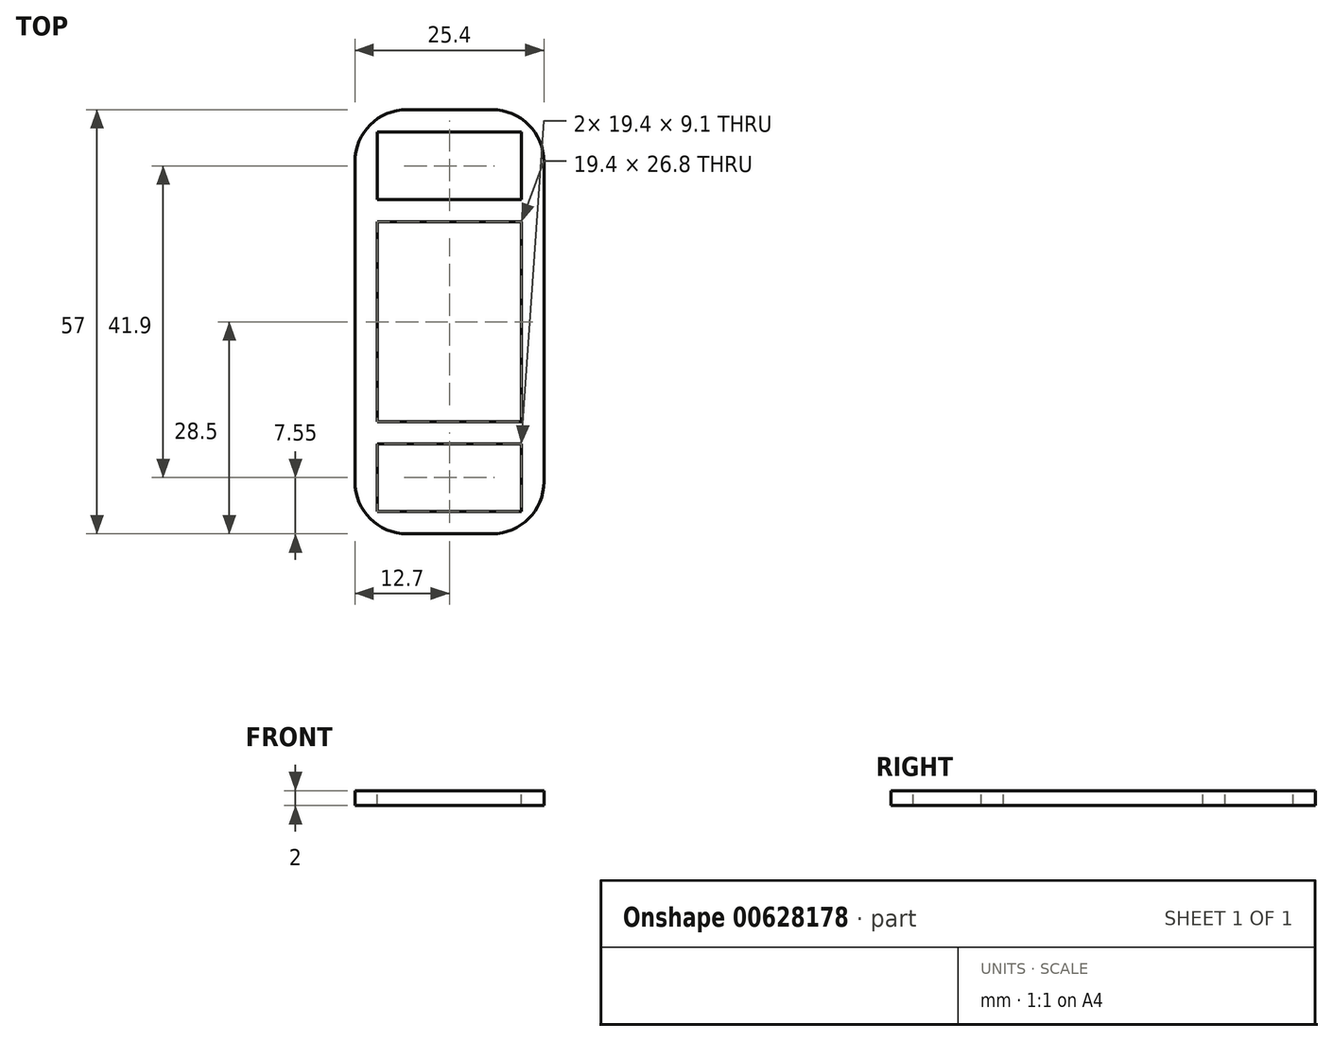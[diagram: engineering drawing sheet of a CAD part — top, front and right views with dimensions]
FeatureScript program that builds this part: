
annotation { "Feature Type Name" : "Feature", "Feature Type Description" : "" }
export const myFeature = defineFeature(function(context is Context, id is Id, definition is map)
    precondition{}
    {
        {
            var Q0;
            Q0=qCreatedBy(makeId("Top.planeOp"),FACE);
            var sketch = newSketch(context, id + "F0", { "sketchPlane" : qUnion([Q0])});
            skLineSegment(sketch, "E0.bottom", {"start": v(-12.7, 28.5) * mm, "end": v(12.7, 28.5) * mm});
            skLineSegment(sketch, "E0.top", {"start": v(-12.7, -28.5) * mm, "end": v(12.7, -28.5) * mm});
            skLineSegment(sketch, "E0.left", {"start": v(-12.7, 28.5) * mm, "end": v(-12.7, -28.5) * mm});
            skLineSegment(sketch, "E0.right", {"start": v(12.7, 28.5) * mm, "end": v(12.7, -28.5) * mm});
            skPoint(sketch, "E0.middle", {"position": v(0, 0) * mm});
            skSolve(sketch);
        }
        {
            var Q0;
            Q0=makeQuery(id+"F0.imprint","IMPRINT",FACE,{"disambiguationData":[TD([[makeQuery(id+"F0.imprint","IMPRINT",EDGE,{"derivedFrom":sQuery(id+"F0.wireOp",EDGE,"E0.bottom")}),-1.0]])]});
            extrude(context, id + "F1", {"entities" : qUnion([Q0]), "depth" : 2 * mm, "offsetDistance" : 25 * mm});
        }
        {
            var Q0;
            Q0=makeQuery(id+"F1.opExtrude","CAP_FACE",FACE,{"disambiguationData":[OSD([sQuery(id+"F0.wireOp",EDGE,"E0.bottom"),sQuery(id+"F0.wireOp",EDGE,"E0.top"),sQuery(id+"F0.wireOp",EDGE,"E0.left"),sQuery(id+"F0.wireOp",EDGE,"E0.right")])],"isStart":false});
            var sketch = newSketch(context, id + "F2", { "sketchPlane" : qUnion([Q0])});
            skPoint(sketch, "E1", {"position": v(-9.7, 13.4) * mm});
            skPoint(sketch, "E2", {"position": v(9.7, 25.5) * mm});
            skPoint(sketch, "E3", {"position": v(-9.7, 16.4) * mm});
            skLineSegment(sketch, "E4.bottom", {"start": v(-9.7, 16.4) * mm, "end": v(9.7, 16.4) * mm});
            skLineSegment(sketch, "E4.top", {"start": v(-9.7, 25.5) * mm, "end": v(9.7, 25.5) * mm});
            skLineSegment(sketch, "E4.left", {"start": v(-9.7, 16.4) * mm, "end": v(-9.7, 25.5) * mm});
            skLineSegment(sketch, "E4.right", {"start": v(9.7, 16.4) * mm, "end": v(9.7, 25.5) * mm});
            skPoint(sketch, "E5", {"position": v(-9.7, -13.4) * mm});
            skPoint(sketch, "E6", {"position": v(-9.7, -16.4) * mm});
            skPoint(sketch, "E7", {"position": v(9.7, -25.5) * mm});
            skLineSegment(sketch, "E8.bottom", {"start": v(9.7, -25.5) * mm, "end": v(-9.7, -25.5) * mm});
            skLineSegment(sketch, "E8.top", {"start": v(9.7, -16.4) * mm, "end": v(-9.7, -16.4) * mm});
            skLineSegment(sketch, "E8.left", {"start": v(9.7, -25.5) * mm, "end": v(9.7, -16.4) * mm});
            skLineSegment(sketch, "E8.right", {"start": v(-9.7, -25.5) * mm, "end": v(-9.7, -16.4) * mm});
            skPoint(sketch, "E9", {"position": v(9.7, -13.4) * mm});
            skLineSegment(sketch, "E10.bottom", {"start": v(9.7, -13.4) * mm, "end": v(-9.7, -13.4) * mm});
            skLineSegment(sketch, "E10.top", {"start": v(9.7, 13.4) * mm, "end": v(-9.7, 13.4) * mm});
            skLineSegment(sketch, "E10.left", {"start": v(9.7, -13.4) * mm, "end": v(9.7, 13.4) * mm});
            skLineSegment(sketch, "E10.right", {"start": v(-9.7, -13.4) * mm, "end": v(-9.7, 13.4) * mm});
            skSolve(sketch);
        }
        {
            var Q0;
            Q0=makeQuery(id+"F2.imprint","IMPRINT",FACE,{"disambiguationData":[TD([[makeQuery(id+"F2.imprint","IMPRINT",EDGE,{"derivedFrom":sQuery(id+"F2.wireOp",EDGE,"E4.bottom")}),1.0]])]});
            var Q1;
            Q1=makeQuery(id+"F2.imprint","IMPRINT",FACE,{"disambiguationData":[TD([[makeQuery(id+"F2.imprint","IMPRINT",EDGE,{"derivedFrom":sQuery(id+"F2.wireOp",EDGE,"E10.bottom")}),-1.0]])]});
            var Q2;
            Q2=makeQuery(id+"F2.imprint","IMPRINT",FACE,{"disambiguationData":[TD([[makeQuery(id+"F2.imprint","IMPRINT",EDGE,{"derivedFrom":sQuery(id+"F2.wireOp",EDGE,"E8.bottom")}),-1.0]])]});
            extrude(context, id + "F3", {"entities" : qUnion([Q0, Q1, Q2]), "operationType" : NewBodyOperationType.REMOVE, "endBound" : BoundingType.THROUGH_ALL, "oppositeDirection" : true, "depth" : 25 * mm, "offsetDistance" : 25 * mm});
        }
        {
            var Q0;
            Q0=makeQuery(id+"F1.opExtrude","SWEPT_EDGE",EDGE,{"disambiguationData":[OSD([sQuery(id+"F0.wireOp",EDGE,"E0.bottom"),sQuery(id+"F0.wireOp",EDGE,"E0.right")])]});
            var Q1;
            Q1=makeQuery(id+"F1.opExtrude","SWEPT_EDGE",EDGE,{"disambiguationData":[OSD([sQuery(id+"F0.wireOp",EDGE,"E0.top"),sQuery(id+"F0.wireOp",EDGE,"E0.right")])]});
            var Q2;
            Q2=makeQuery(id+"F1.opExtrude","SWEPT_EDGE",EDGE,{"disambiguationData":[OSD([sQuery(id+"F0.wireOp",EDGE,"E0.top"),sQuery(id+"F0.wireOp",EDGE,"E0.left")])]});
            var Q3;
            Q3=makeQuery(id+"F1.opExtrude","SWEPT_EDGE",EDGE,{"disambiguationData":[OSD([sQuery(id+"F0.wireOp",EDGE,"E0.bottom"),sQuery(id+"F0.wireOp",EDGE,"E0.left")])]});
            fillet(context, id + "F4", {"entities" : qUnion([Q0, Q1, Q2, Q3]), "radius" : 7 * mm, "tangentPropagation" : true, "allowEdgeOverflow" : false});
        }
    });
